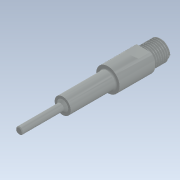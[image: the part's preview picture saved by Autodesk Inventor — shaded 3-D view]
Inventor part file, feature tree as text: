
AUTODESK INVENTOR PART (.ipt)
format: ipt  version: 2021 (Build 250183000, 183)  size: 234,496 bytes
history: native  units: mm
features: other x1, extrude x1, sketch x1, thread x1
ambient origin geometry x8: Origin, YZ Plane, XZ Plane, XY Plane, X Axis, Y Axis, Z Axis, Center Point
bodies: Body1 (feature_tree)
feature tree (4):
  other  "Sólido1"
  extrude  "Extrusión1"  Depth=10.0mm TaperAngle=0.0deg
  sketch  "Boceto1"  dims[d0=14.0mm d1=10.0mm d2=0.0mm]
  thread  "Rosca1"  [1 undecoded]
note: 1 required parameter value undecoded (feature->parameter linkage not recoverable at this tier; creation-order binding heuristic only, values carry confidence <= 0.55)
